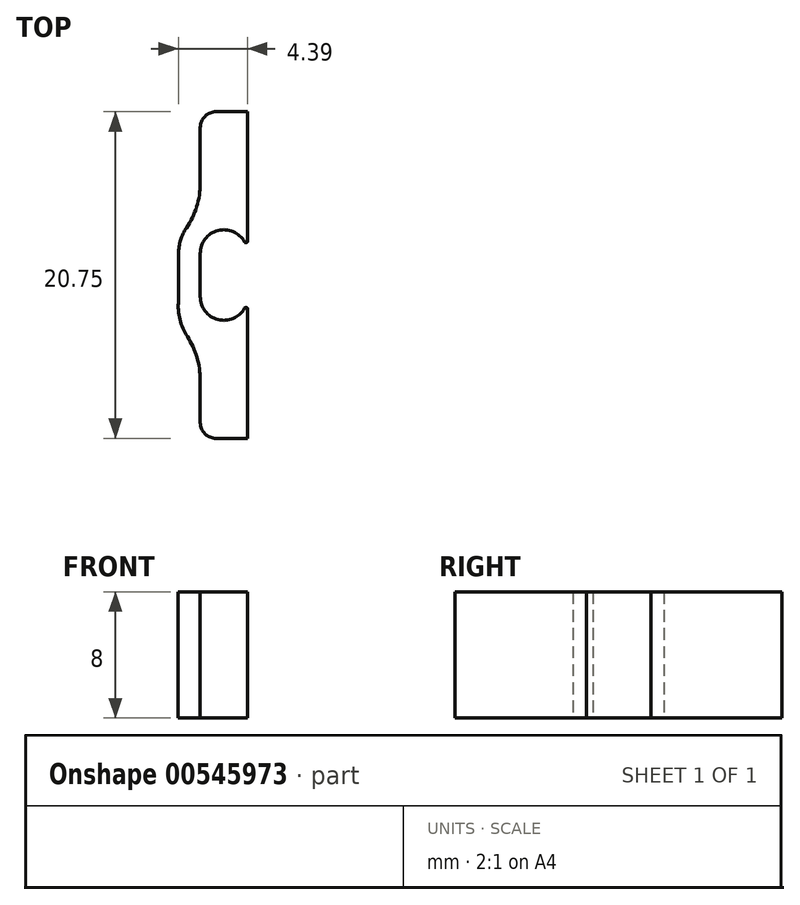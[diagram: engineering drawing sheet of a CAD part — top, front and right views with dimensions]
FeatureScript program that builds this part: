
annotation { "Feature Type Name" : "Feature", "Feature Type Description" : "" }
export const myFeature = defineFeature(function(context is Context, id is Id, definition is map)
    precondition{}
    {
        {
            var Q0;
            Q0=qCreatedBy(makeId("Top.planeOp"),FACE);
            var sketch = newSketch(context, id + "F0", { "sketchPlane" : qUnion([Q0])});
            skLineSegment(sketch, "E0.left", {"start": v(0, 0) * mm, "end": v(0, -2.75) * mm});
            skLineSegment(sketch, "E0.right", {"start": v(3, 0) * mm, "end": v(3, -2.75) * mm});
            skArc(sketch, "E1", {"start": v(3, 0) * mm, "mid": v(1.5, 1.5) * mm, "end": v(0, 0) * mm});
            skArc(sketch, "E2", {"start": v(3, -2.75) * mm, "mid": v(1.5, -4.25) * mm, "end": v(0, -2.75) * mm});
            skArc(sketch, "E3.0", {"start": v(0, 2.45) * mm, "mid": v(-1, 1.4) * mm, "end": v(-1.38, 0) * mm});
            skLineSegment(sketch, "E3.3", {"start": v(-1.38, 0) * mm, "end": v(-1.38, -3) * mm});
            skLineSegment(sketch, "E4", {"start": v(3, 0) * mm, "end": v(3, 9) * mm});
            skLineSegment(sketch, "E5", {"start": v(3, 9) * mm, "end": v(0, 9) * mm});
            skLineSegment(sketch, "E6", {"start": v(0, 9) * mm, "end": v(0, 2.45) * mm});
            skLineSegment(sketch, "E7", {"start": v(3, -2.75) * mm, "end": v(3, -11.75) * mm});
            skLineSegment(sketch, "E8", {"start": v(3, -11.75) * mm, "end": v(0, -11.75) * mm});
            skLineSegment(sketch, "E9", {"start": v(0, -11.75) * mm, "end": v(0, -6.16) * mm});
            skArc(sketch, "E10.trimOffspring", {"start": v(0, -6.16) * mm, "mid": v(-1.1, -4.76) * mm, "end": v(-1.37, -3) * mm});
            skSolve(sketch);
        }
        {
            var Q0;
            Q0=makeQuery(id+"F0.imprint","IMPRINT",FACE,{"disambiguationData":[TD([[makeQuery(id+"F0.imprint","IMPRINT",EDGE,{"derivedFrom":sQuery(id+"F0.wireOp",EDGE,"E0.left")}),-1.0]])]});
            extrude(context, id + "F1", {"entities" : qUnion([Q0]), "depth" : 8 * mm, "offsetDistance" : 25 * mm});
        }
        {
            var Q0;
            Q0=makeQuery(id+"F1.opExtrude","SWEPT_EDGE",EDGE,{"disambiguationData":[OSD([sQuery(id+"F0.wireOp",EDGE,"E0.right"),sQuery(id+"F0.wireOp",EDGE,"E1"),sQuery(id+"F0.wireOp",EDGE,"E4")])]});
            var Q1;
            Q1=makeQuery(id+"F1.opExtrude","SWEPT_EDGE",EDGE,{"disambiguationData":[OSD([sQuery(id+"F0.wireOp",EDGE,"E0.right"),sQuery(id+"F0.wireOp",EDGE,"E2"),sQuery(id+"F0.wireOp",EDGE,"E7")])]});
            fillet(context, id + "F2", {"entities" : qUnion([Q0, Q1]), "radius" : 0.1 * mm, "tangentPropagation" : true, "allowEdgeOverflow" : false});
        }
        {
            var Q0;
            Q0=makeQuery(id+"F1.opExtrude","SWEPT_EDGE",EDGE,{"disambiguationData":[OSD([sQuery(id+"F0.wireOp",EDGE,"E5"),sQuery(id+"F0.wireOp",EDGE,"E6")])]});
            var Q1;
            Q1=makeQuery(id+"F1.opExtrude","SWEPT_EDGE",EDGE,{"disambiguationData":[OSD([sQuery(id+"F0.wireOp",EDGE,"E8"),sQuery(id+"F0.wireOp",EDGE,"E9")])]});
            fillet(context, id + "F3", {"entities" : qUnion([Q0, Q1]), "radius" : 1 * mm, "tangentPropagation" : true, "allowEdgeOverflow" : false});
        }
        {
            var Q0;
            Q0=makeQuery(id+"F1.opExtrude","SWEPT_EDGE",EDGE,{"disambiguationData":[OSD([sQuery(id+"F0.wireOp",EDGE,"E3.0"),sQuery(id+"F0.wireOp",EDGE,"E6")])]});
            var Q1;
            Q1=makeQuery(id+"F1.opExtrude","SWEPT_EDGE",EDGE,{"disambiguationData":[OSD([sQuery(id+"F0.wireOp",EDGE,"E9"),sQuery(id+"F0.wireOp",EDGE,"E10.trimOffspring")])]});
            fillet(context, id + "F4", {"entities" : qUnion([Q0, Q1]), "radius" : 5 * mm, "tangentPropagation" : true, "allowEdgeOverflow" : false});
        }
    });
